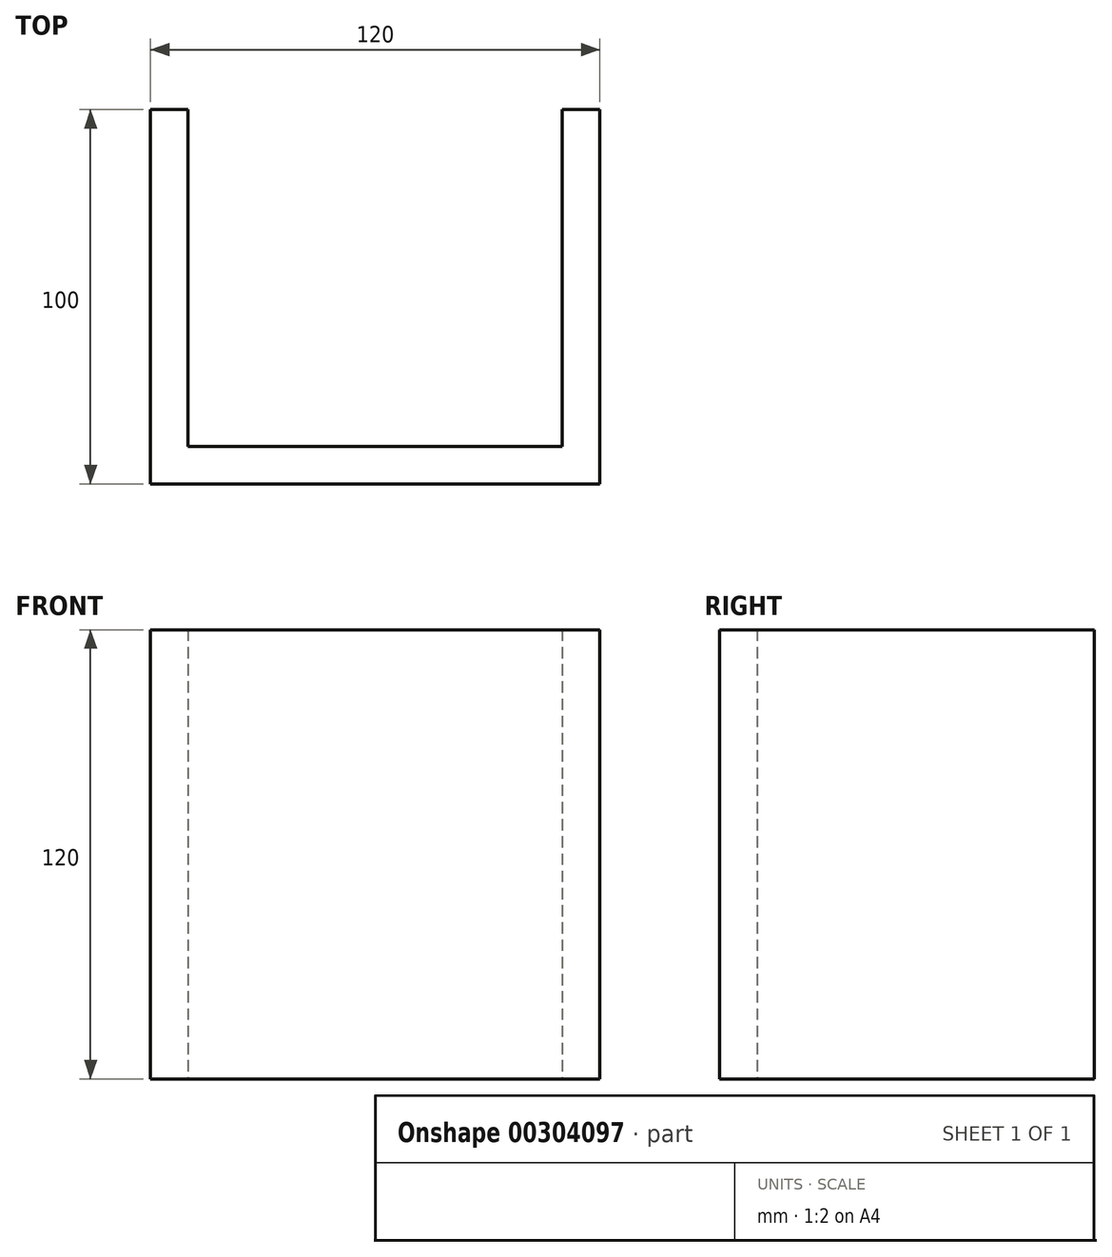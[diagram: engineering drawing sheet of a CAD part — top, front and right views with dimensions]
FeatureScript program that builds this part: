
annotation { "Feature Type Name" : "Feature", "Feature Type Description" : "" }
export const myFeature = defineFeature(function(context is Context, id is Id, definition is map)
    precondition{}
    {
        {
            var Q0;
            Q0=qCreatedBy(makeId("Top.planeOp"),FACE);
            var sketch = newSketch(context, id + "F0", { "sketchPlane" : qUnion([Q0])});
            skLineSegment(sketch, "E0", {"start": v(-55.05, -62.98) * mm, "end": v(64.95, -62.98) * mm});
            skLineSegment(sketch, "E1", {"start": v(64.95, -62.98) * mm, "end": v(64.95, 37.02) * mm});
            skLineSegment(sketch, "E2", {"start": v(64.95, 37.02) * mm, "end": v(54.95, 37.02) * mm});
            skLineSegment(sketch, "E3", {"start": v(54.95, 37.02) * mm, "end": v(54.95, -52.98) * mm});
            skLineSegment(sketch, "E4", {"start": v(54.95, -52.98) * mm, "end": v(-45.05, -52.98) * mm});
            skLineSegment(sketch, "E5", {"start": v(-45.05, -52.98) * mm, "end": v(-45.05, 37.02) * mm});
            skLineSegment(sketch, "E6", {"start": v(-45.05, 37.02) * mm, "end": v(-55.05, 37.02) * mm});
            skLineSegment(sketch, "E7", {"start": v(-55.05, 37.02) * mm, "end": v(-55.05, -62.98) * mm});
            skSolve(sketch);
        }
        {
            var Q0;
            Q0=makeQuery(id+"F0.imprint","IMPRINT",FACE,{"disambiguationData":[TD([[makeQuery(id+"F0.imprint","IMPRINT",EDGE,{"derivedFrom":sQuery(id+"F0.wireOp",EDGE,"E0")}),1.0]])]});
            extrude(context, id + "F1", {"entities" : qUnion([Q0]), "depth" : 120 * mm, "offsetDistance" : 25 * mm});
        }
    });
